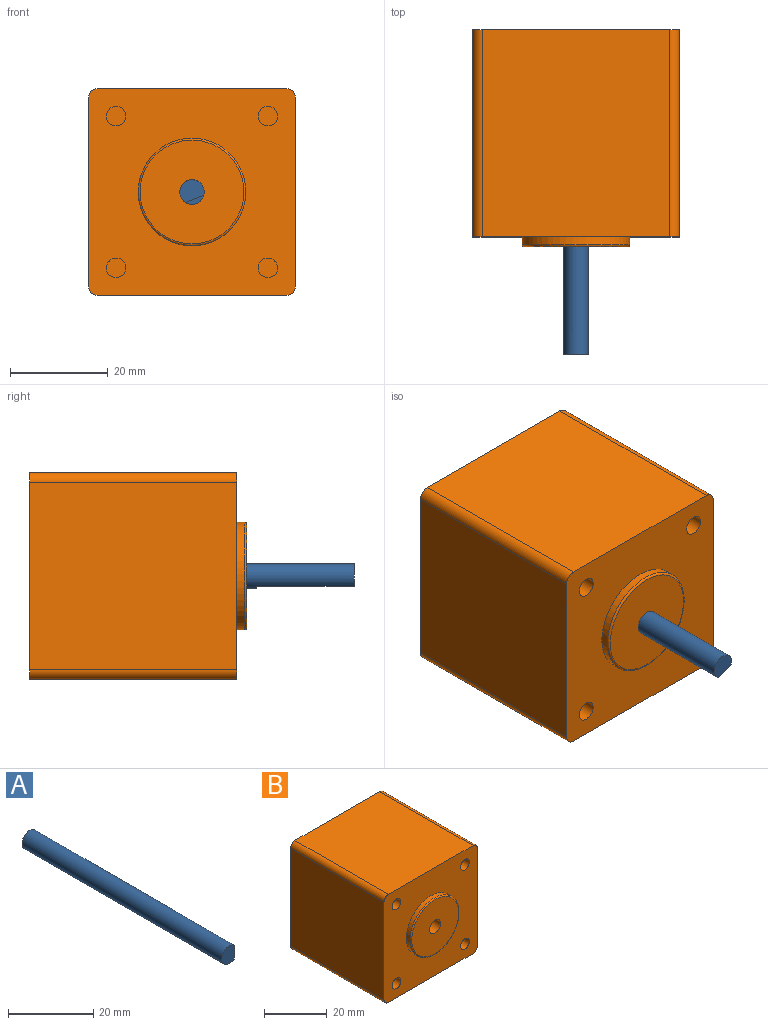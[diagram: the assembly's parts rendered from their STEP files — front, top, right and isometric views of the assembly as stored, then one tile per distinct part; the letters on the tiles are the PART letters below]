
ASSEMBLY  parts=2 mates=1
PART A: 5 faces, bbox 5x66.3x5 mm
  f0: plane 5x4mm, normal (0,-1,0), area 16.8mm2, adj f2,f3
  f1: plane 5x5mm, normal (0,1,0), area 19.6mm2, adj f2
  f2: cylinder r=2.5mm len=66.3mm, axis (0,1,0), area 948.7mm2, adj f0,f1,f3,f4
  f3: plane 20x4mm, normal (1,0,0), area 80mm2, adj f0,f2,f4
  f4: plane 4x1mm, normal (0,-1,0), area 2.8mm2, adj f2,f3
PART B: 22 faces, bbox 42.3x44.3x42.3 mm
  f0: plane 42.3x38.3mm, normal (0,0,-1), area 1620.1mm2, adj f5,f6,f18,f21
  f1: plane 42.3x38.3mm, normal (1,0,0), area 1620.1mm2, adj f5,f6,f18,f19
  f2: plane 42.3x38.3mm, normal (0,0,1), area 1620.1mm2, adj f5,f6,f19,f20
  f3: cylinder r=2.5mm len=44.3mm, axis (0,-1,0), area 695.9mm2, adj f5,f8
  f4: plane 42.3x38.3mm, normal (-1,0,0), area 1620.1mm2, adj f5,f6,f20,f21
  f5: plane 42.3x42.3mm, normal (0,1,0), area 1766.2mm2, adj f0,f1,f2,f3,f4,f18,f19,f20
  f6: plane 42.3x42.3mm, normal (0,-1,0), area 1355.5mm2, adj f0,f1,f2,f4,f7,f9,f11,f13
  f7: cylinder r=11mm len=22mm, axis (0,1,0), area 110.6mm2, adj f6,f17
  f8: plane 21.2x21.2mm, normal (0,-1,0), area 333.4mm2, adj f3,f17
  f9: cylinder r=2mm len=10mm, axis (0,-1,0), area 125.7mm2, adj f6,f10
  f10: plane 4x4mm, normal (0,-1,0), area 12.6mm2, adj f9
  f11: cylinder r=2mm len=10mm, axis (0,-1,0), area 125.7mm2, adj f6,f12
  f12: plane 4x4mm, normal (0,-1,0), area 12.6mm2, adj f11
  f13: cylinder r=2mm len=10mm, axis (0,-1,0), area 125.7mm2, adj f6,f14
  f14: plane 4x4mm, normal (0,-1,0), area 12.6mm2, adj f13
  f15: cylinder r=2mm len=10mm, axis (0,-1,0), area 125.7mm2, adj f6,f16
  f16: plane 4x4mm, normal (0,-1,0), area 12.6mm2, adj f15
  f17: torus R=10.6mm, axis (0,-1,0), area 42.9mm2, adj f7,f8
  f18: cylinder r=2mm len=42.3mm, axis (0,1,0), area 132.9mm2, adj f0,f1,f5,f6
  f19: cylinder r=2mm len=42.3mm, axis (0,-1,0), area 132.9mm2, adj f1,f2,f5,f6
  f20: cylinder r=2mm len=42.3mm, axis (0,1,0), area 132.9mm2, adj f2,f4,f5,f6
  f21: cylinder r=2mm len=42.3mm, axis (0,-1,0), area 132.9mm2, adj f0,f4,f5,f6
PLACE A rot(axis=(0,1,0),68.4deg) t=(0.27,0.2,0.01)mm
PLACE B t=(0.27,0.2,0.01)mm fixed
MATE revolute B.f3 <-> A.f2  axis (0,-1,0) through (0.27,35.76,0.01)mm
